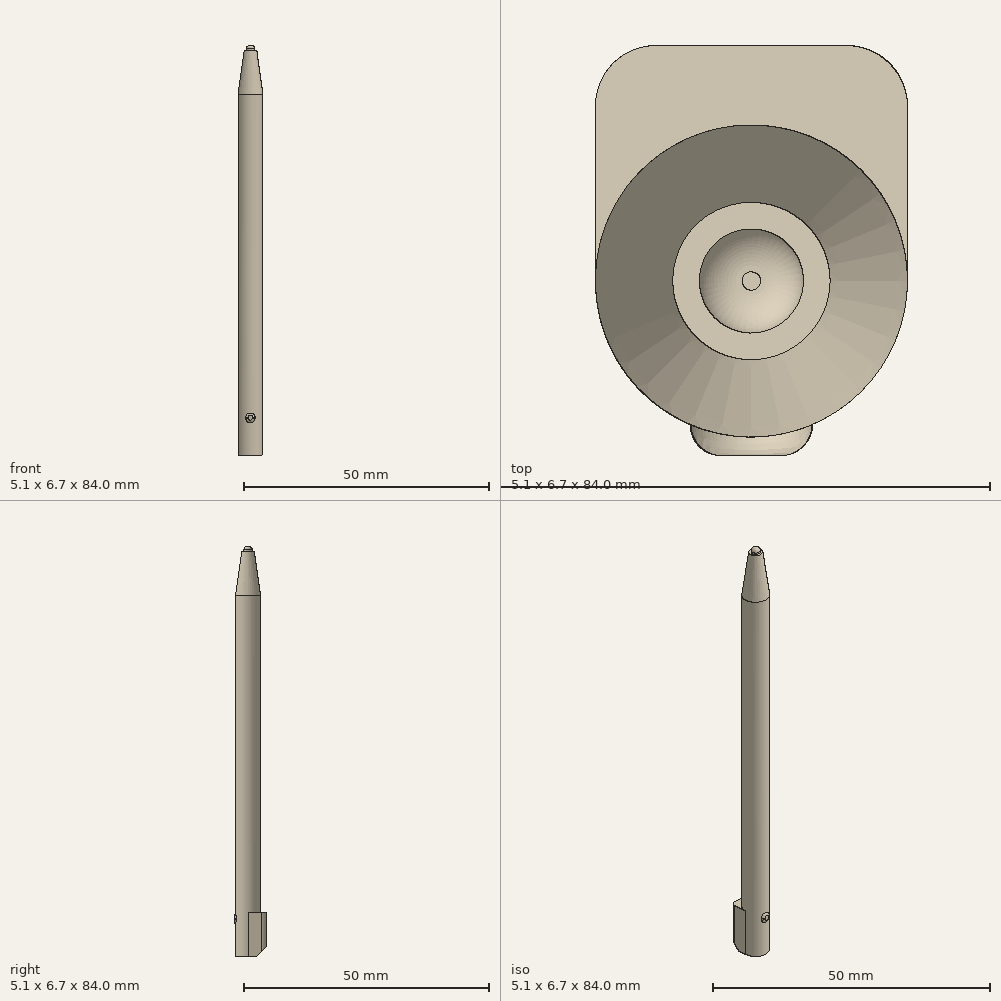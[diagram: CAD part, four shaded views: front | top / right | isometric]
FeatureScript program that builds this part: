
annotation { "Feature Type Name" : "Feature", "Feature Type Description" : "" }
export const myFeature = defineFeature(function(context is Context, id is Id, definition is map)
    precondition{}
    {
        {
            var Q0;
            Q0=qCreatedBy(makeId("Top.planeOp"),FACE);
            var sketch = newSketch(context, id + "F0", { "sketchPlane" : qUnion([Q0])});
            skCircle(sketch, "E0", {"center": v(0, 0) * mm, "radius": 2.55 * mm});
            skLineSegment(sketch, "E1", {"start": v(-2.55, 3.85) * mm, "end": v(2.55, 3.85) * mm});
            skLineSegment(sketch, "E2", {"start": v(2.55, 3.85) * mm, "end": v(2.55, 0) * mm});
            skLineSegment(sketch, "E3", {"start": v(-2.55, 0) * mm, "end": v(-2.55, 3.85) * mm});
            skArc(sketch, "E4", {"start": v(-2.55, 0) * mm, "mid": v(0, -2.55) * mm, "end": v(2.55, 0) * mm});
            skCircle(sketch, "E5", {"center": v(0, 0) * mm, "radius": 0.85 * mm});
            skPoint(sketch, "E6.startSnap0", {"position": v(0, -2.55) * mm});
            skLineSegment(sketch, "E7", {"start": v(0, -2.65) * mm, "end": v(0, -3.76) * mm, "construction": true});
            skSolve(sketch);
        }
        {
            var Q0;
            Q0=makeQuery(id+"F0.imprint","IMPRINT",FACE,{"disambiguationData":[TD([[makeQuery(id+"F0.imprint","IMPRINT",EDGE,{"derivedFrom":sQuery(id+"F0.wireOp",EDGE,"E1")}),-1.0]])]});
            var Q1;
            Q1=makeQuery(id+"F0.imprint","IMPRINT",FACE,{"disambiguationData":[TD([[makeQuery(id+"F0.imprint","IMPRINT",EDGE,{"derivedFrom":sQuery(id+"F0.wireOp",EDGE,"E5")}),1.0]])]});
            var Q2;
            Q2=makeQuery(id+"F0.imprint","IMPRINT",FACE,{"disambiguationData":[TD([[makeQuery(id+"F0.imprint","IMPRINT",EDGE,{"derivedFrom":sQuery(id+"F0.wireOp",EDGE,"E5")}),-1.0]])]});
            extrude(context, id + "F1", {"entities" : qUnion([Q0, Q1, Q2]), "oppositeDirection" : true, "depth" : 9 * mm, "offsetDistance" : 25 * mm});
        }
        {
            var Q0;
            {var subQ0=sQuery(id+"F0.wireOp",EDGE,"E0");var subQ1=makeQuery(id+"F0.imprint","INTERSECT",VERTEX,{"derivedFrom":[subQ0,sQuery(id+"F0.wireOp",EDGE,"E2")]});Q0=makeQuery(id+"F0.imprint","IMPRINT",FACE,{"disambiguationData":[TD([[makeQuery(id+"F0.imprint","IMPRINT",EDGE,{"disambiguationData":[TD([[subQ1,1.0]])],"derivedFrom":subQ0}),1.0]])]});}
            var Q1;
            Q1=makeQuery(id+"F0.imprint","IMPRINT",FACE,{"disambiguationData":[TD([[makeQuery(id+"F0.imprint","IMPRINT",EDGE,{"derivedFrom":sQuery(id+"F0.wireOp",EDGE,"E5")}),1.0]])]});
            extrude(context, id + "F2", {"entities" : qUnion([Q0, Q1]), "operationType" : NewBodyOperationType.ADD, "depth" : 65 * mm, "offsetDistance" : 25 * mm});
        }
        {
            var Q0;
            Q0=makeQuery(id+"F2.opExtrude","CAP_FACE",FACE,{"disambiguationData":[OSD([sQuery(id+"F0.wireOp",EDGE,"E0")])],"isStart":false});
            extrude(context, id + "F3", {"entities" : qUnion([Q0]), "operationType" : NewBodyOperationType.ADD, "depth" : 9 * mm, "offsetDistance" : 25 * mm, "hasDraft" : true, "draftAngle" : 8 * degree, "draftPullDirection" : true});
        }
        {
            var Q0;
            Q0=makeQuery(id+"F1.opExtrude","SWEPT_EDGE",EDGE,{"disambiguationData":[OSD([sQuery(id+"F0.wireOp",EDGE,"E1"),sQuery(id+"F0.wireOp",EDGE,"E2")])]});
            var Q1;
            Q1=makeQuery(id+"F1.opExtrude","SWEPT_EDGE",EDGE,{"disambiguationData":[OSD([sQuery(id+"F0.wireOp",EDGE,"E1"),sQuery(id+"F0.wireOp",EDGE,"E3")])]});
            fillet(context, id + "F4", {"entities" : qUnion([Q0, Q1]), "radius" : 1 * mm, "tangentPropagation" : true, "allowEdgeOverflow" : false});
        }
        {
            var Q0;
            Q0=makeQuery(id+"F0.imprint","IMPRINT",FACE,{"disambiguationData":[TD([[makeQuery(id+"F0.imprint","IMPRINT",EDGE,{"derivedFrom":sQuery(id+"F0.wireOp",EDGE,"E5")}),1.0]])]});
            extrude(context, id + "F5", {"entities" : qUnion([Q0]), "operationType" : NewBodyOperationType.ADD, "depth" : 75 * mm, "offsetDistance" : 25 * mm});
        }
        {
            var Q0;
            Q0=makeQuery(id+"F5.opExtrude","CAP_EDGE",EDGE,{"disambiguationData":[OSD([sQuery(id+"F0.wireOp",EDGE,"E5")])],"isStart":false});
            fillet(context, id + "F6", {"entities" : qUnion([Q0]), "radius" : 0.7 * mm, "tangentPropagation" : true, "allowEdgeOverflow" : false});
        }
        {
            var Q0;
            Q0=makeQuery(id+"F1.opExtrude","SWEPT_FACE",FACE,{"disambiguationData":[OSD([sQuery(id+"F0.wireOp",EDGE,"E1")])]});
            var sketch = newSketch(context, id + "F7", { "sketchPlane" : qUnion([Q0])});
            skCircle(sketch, "E8", {"center": v(0, -1.3) * mm, "radius": 1 * mm});
            skSolve(sketch);
        }
        {
            var Q0;
            Q0=qSketchRegion(id+"F7",true);
            var Q1;
            {var subQ0=sQuery(id+"F0.wireOp",EDGE,"E0");Q1=makeQuery(id+"F2.boolean.opBoolean","MERGE",FACE,{"derivedFrom":[makeQuery(id+"F1.opExtrude","SWEPT_FACE",FACE,{"disambiguationData":[OSD([subQ0])]}),makeQuery(id+"F2.opExtrude","SWEPT_FACE",FACE,{"disambiguationData":[OSD([subQ0])]})]});}
            extrude(context, id + "F8", {"entities" : qUnion([Q0]), "operationType" : NewBodyOperationType.ADD, "oppositeDirection" : true, "depth" : 6.7 * mm, "offsetDistance" : 25 * mm, "hasSecondDirection" : true, "secondDirectionBound" : SecondDirectionBoundingType.UP_TO_SURFACE, "secondDirectionOppositeDirection" : true, "secondDirectionDepth" : 25 * mm, "secondDirectionBoundEntityFace" : qUnion([Q1])});
        }
        {
            var Q0;
            {var subQ0=sQuery(id+"F7.wireOp",EDGE,"E8");var subQ1=makeQuery(id+"F1.opExtrude","SWEPT_EDGE",EDGE,{"disambiguationData":[OSD([sQuery(id+"F0.wireOp",EDGE,"E0"),sQuery(id+"F0.wireOp",EDGE,"E2")])]});var subQ2=makeQuery(id+"F7.imprint","INTERSECT",VERTEX,{"disambiguationData":[OD(0.0)],"derivedFrom":[subQ1,subQ0]});Q0=makeQuery(id+"F8.opExtrude","CAP_EDGE",EDGE,{"disambiguationData":[OSD([subQ0]),topologyDisambiguationEdgeConnected([makeQuery(id+"F7.imprint","IMPRINT",EDGE,{"disambiguationData":[TD([[subQ2,1.0]])],"derivedFrom":subQ0})])],"isStart":false});}
            fillet(context, id + "F9", {"entities" : qUnion([Q0]), "radius" : 0.5 * mm, "tangentPropagation" : true, "allowEdgeOverflow" : false});
        }
        {
            var Q0;
            Q0=makeQuery(id+"F1.opExtrude","CAP_EDGE",EDGE,{"disambiguationData":[OSD([sQuery(id+"F0.wireOp",EDGE,"E1")])],"isStart":false});
            chamfer(context, id + "F10", {"entities" : qUnion([Q0]), "width" : 2 * mm});
        }
    });
